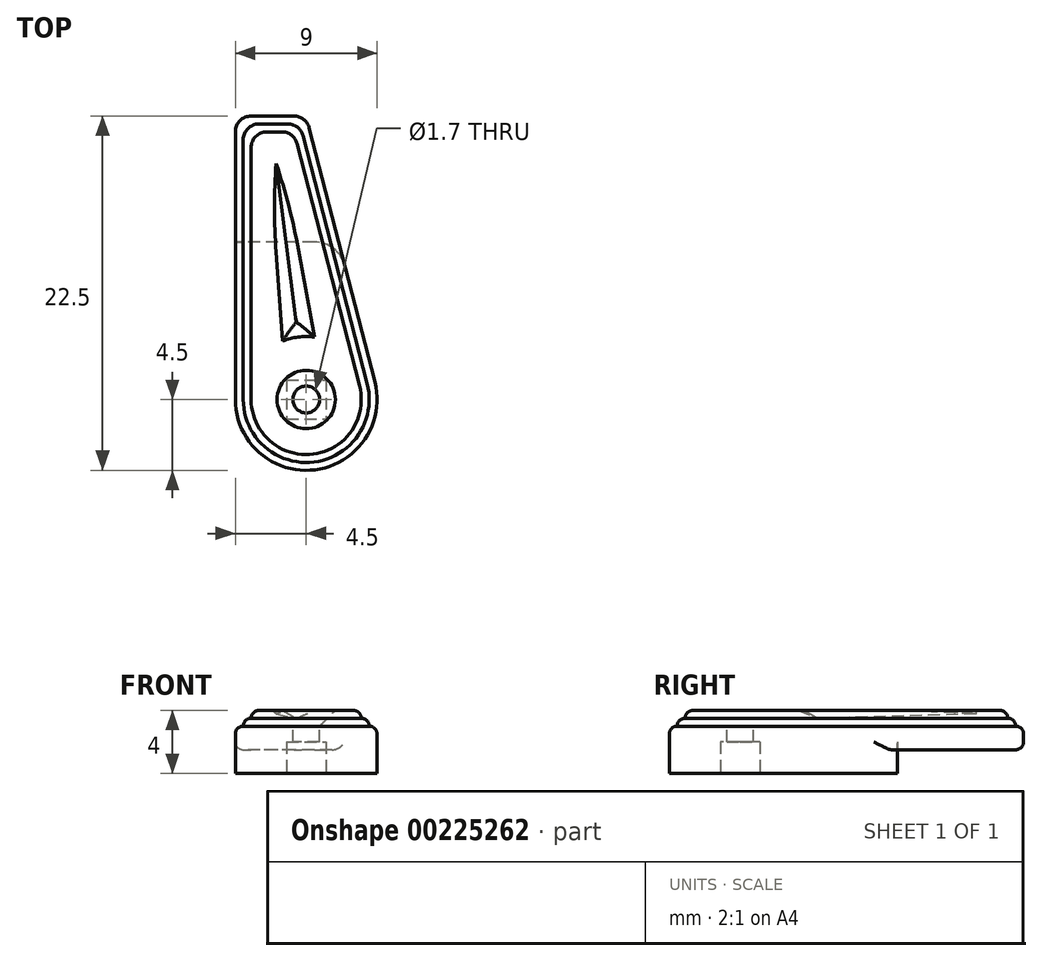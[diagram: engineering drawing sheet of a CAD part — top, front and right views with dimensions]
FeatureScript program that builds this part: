
annotation { "Feature Type Name" : "Feature", "Feature Type Description" : "" }
export const myFeature = defineFeature(function(context is Context, id is Id, definition is map)
    precondition{}
    {
        {
            var Q0;
            Q0=qCreatedBy(makeId("Top.planeOp"),FACE);
            var sketch = newSketch(context, id + "F0", { "sketchPlane" : qUnion([Q0])});
            skLineSegment(sketch, "E0.bottom", {"start": v(-1.25, 1.25) * mm, "end": v(1.25, 1.25) * mm});
            skLineSegment(sketch, "E0.top", {"start": v(-1.25, -1.25) * mm, "end": v(1.25, -1.25) * mm});
            skLineSegment(sketch, "E0.left", {"start": v(-1.25, 1.25) * mm, "end": v(-1.25, -1.25) * mm});
            skLineSegment(sketch, "E0.right", {"start": v(1.25, 1.25) * mm, "end": v(1.25, -1.25) * mm});
            skPoint(sketch, "E0.middle", {"position": v(0, 0) * mm});
            skCircle(sketch, "E1", {"center": v(0, 0) * mm, "radius": 4.5 * mm});
            skLineSegment(sketch, "E2", {"start": v(-4.5, 0) * mm, "end": v(-4.5, 18) * mm});
            skLineSegment(sketch, "E3", {"start": v(-4.5, 18) * mm, "end": v(0, 18) * mm});
            skLineSegment(sketch, "E4", {"start": v(0, 18) * mm, "end": v(4.36, 1.12) * mm});
            skSolve(sketch);
        }
        {
            var Q0;
            Q0 = qSketchRegion(id + "F0", true);
            extrude(context, id + "F1", {"entities" : qUnion([Q0]), "depth" : 3 * mm, "offsetDistance" : 25 * mm});
        }
        {
            var Q0;
            Q0=makeQuery(id+"F1.opExtrude","CAP_FACE",FACE,{"disambiguationData":[OSD([sQuery(id+"F0.wireOp",EDGE,"E0.bottom"),sQuery(id+"F0.wireOp",EDGE,"E0.top"),sQuery(id+"F0.wireOp",EDGE,"E0.left"),sQuery(id+"F0.wireOp",EDGE,"E0.right"),sQuery(id+"F0.wireOp",EDGE,"E1"),sQuery(id+"F0.wireOp",EDGE,"E2"),sQuery(id+"F0.wireOp",EDGE,"E3"),sQuery(id+"F0.wireOp",EDGE,"E4")])],"isStart":false});
            var sketch = newSketch(context, id + "F2", { "sketchPlane" : qUnion([Q0])});
            skCircle(sketch, "E5", {"center": v(0, 0) * mm, "radius": 0.85 * mm});
            skLineSegment(sketch, "E6.0", {"start": v(-3.5, 0) * mm, "end": v(-3.5, 17) * mm});
            skArc(sketch, "E6.1", {"start": v(-3.5, 0) * mm, "mid": v(0.44, -3.47) * mm, "end": v(3.39, 0.87) * mm});
            skLineSegment(sketch, "E6.2", {"start": v(-0.77, 17) * mm, "end": v(3.39, 0.88) * mm});
            skLineSegment(sketch, "E6.3", {"start": v(-3.5, 17) * mm, "end": v(-0.77, 17) * mm});
            skSolve(sketch);
        }
        {
            var Q0;
            Q0 = qSketchRegion(id + "F2", true);
            extrude(context, id + "F3", {"entities" : qUnion([Q0]), "operationType" : NewBodyOperationType.ADD, "oppositeDirection" : true, "depth" : 1 * mm, "offsetDistance" : 25 * mm});
        }
        {
            var Q0;
            Q0=makeQuery(id+"F2.imprint","IMPRINT",FACE,{"disambiguationData":[TD([[makeQuery(id+"F2.imprint","IMPRINT",EDGE,{"derivedFrom":sQuery(id+"F2.wireOp",EDGE,"E6.0")}),-1.0]])]});
            var Q1;
            Q1=makeQuery(id+"F2.imprint","IMPRINT",FACE,{"disambiguationData":[TD([[makeQuery(id+"F2.imprint","IMPRINT",EDGE,{"derivedFrom":sQuery(id+"F2.wireOp",EDGE,"E5")}),-1.0]])]});
            extrude(context, id + "F4", {"entities" : qUnion([Q0, Q1]), "operationType" : NewBodyOperationType.ADD, "depth" : 1 * mm, "offsetDistance" : 25 * mm});
        }
        {
            var Q0;
            Q0=makeQuery(id+"F3.boolean.opBoolean","MERGE",FACE,{"derivedFrom":[makeQuery(id+"F1.opExtrude","CAP_FACE",FACE,{"disambiguationData":[OSD([sQuery(id+"F0.wireOp",EDGE,"E0.bottom"),sQuery(id+"F0.wireOp",EDGE,"E0.top"),sQuery(id+"F0.wireOp",EDGE,"E0.left"),sQuery(id+"F0.wireOp",EDGE,"E0.right"),sQuery(id+"F0.wireOp",EDGE,"E1"),sQuery(id+"F0.wireOp",EDGE,"E2"),sQuery(id+"F0.wireOp",EDGE,"E3"),sQuery(id+"F0.wireOp",EDGE,"E4")])],"isStart":false}),makeQuery(id+"F3.opExtrude","CAP_FACE",FACE,{"disambiguationData":[OSD([sQuery(id+"F2.wireOp",EDGE,"E5"),sQuery(id+"F2.wireOp",EDGE,"E6.0"),sQuery(id+"F2.wireOp",EDGE,"E6.1"),sQuery(id+"F2.wireOp",EDGE,"E6.2"),sQuery(id+"F2.wireOp",EDGE,"E6.3")])],"isStart":true})]});
            var sketch = newSketch(context, id + "F5", { "sketchPlane" : qUnion([Q0])});
            skLineSegment(sketch, "E7.0", {"start": v(-0.39, 17.5) * mm, "end": v(3.87, 1) * mm});
            skLineSegment(sketch, "E7.1", {"start": v(-4, 17.5) * mm, "end": v(-0.39, 17.5) * mm});
            skLineSegment(sketch, "E7.2", {"start": v(-4, 0) * mm, "end": v(-4, 17.5) * mm});
            skArc(sketch, "E7.3", {"start": v(-4, 0) * mm, "mid": v(0.5, -3.97) * mm, "end": v(3.87, 1) * mm});
            skCircle(sketch, "E8", {"center": v(0, 0) * mm, "radius": 1 * mm});
            skSolve(sketch);
        }
        {
            var Q0;
            Q0 = qSketchRegion(id + "F5", true);
            extrude(context, id + "F6", {"entities" : qUnion([Q0]), "operationType" : NewBodyOperationType.ADD, "depth" : 0.5 * mm, "offsetDistance" : 25 * mm});
        }
        {
            var Q0;
            Q0=makeQuery(id+"F1.opExtrude","SWEPT_EDGE",EDGE,{"disambiguationData":[OSD([sQuery(id+"F0.wireOp",EDGE,"E2"),sQuery(id+"F0.wireOp",EDGE,"E3")])]});
            var Q1;
            Q1=makeQuery(id+"F1.opExtrude","SWEPT_EDGE",EDGE,{"disambiguationData":[OSD([sQuery(id+"F0.wireOp",EDGE,"E3"),sQuery(id+"F0.wireOp",EDGE,"E4")])]});
            var Q2;
            Q2=makeQuery(id+"F6.opExtrude","SWEPT_EDGE",EDGE,{"disambiguationData":[OSD([sQuery(id+"F5.wireOp",EDGE,"E7.1"),sQuery(id+"F5.wireOp",EDGE,"E7.2")])]});
            var Q3;
            Q3=makeQuery(id+"F4.opExtrude","SWEPT_EDGE",EDGE,{"disambiguationData":[OSD([sQuery(id+"F2.wireOp",EDGE,"E6.0"),sQuery(id+"F2.wireOp",EDGE,"E6.3")])]});
            var Q4;
            Q4=makeQuery(id+"F6.opExtrude","SWEPT_EDGE",EDGE,{"disambiguationData":[OSD([sQuery(id+"F5.wireOp",EDGE,"E7.0"),sQuery(id+"F5.wireOp",EDGE,"E7.1")])]});
            var Q5;
            Q5=makeQuery(id+"F4.opExtrude","SWEPT_EDGE",EDGE,{"disambiguationData":[OSD([sQuery(id+"F2.wireOp",EDGE,"E6.2"),sQuery(id+"F2.wireOp",EDGE,"E6.3")])]});
            fillet(context, id + "F7", {"entities" : qUnion([Q0, Q1, Q2, Q3, Q4, Q5]), "radius" : 1 * mm, "tangentPropagation" : true, "allowEdgeOverflow" : false});
        }
        {
            var Q0;
            Q0=makeQuery(id+"F1.opExtrude","SWEPT_FACE",FACE,{"disambiguationData":[OSD([sQuery(id+"F0.wireOp",EDGE,"E2")])]});
            var sketch = newSketch(context, id + "F8", { "sketchPlane" : qUnion([Q0])});
            skPoint(sketch, "E9.oppositeSnap0", {"position": v(-17, 1.5) * mm});
            skLineSegment(sketch, "E9.bottom", {"start": v(-18, 0) * mm, "end": v(-10, 0) * mm});
            skLineSegment(sketch, "E9.top", {"start": v(-18, 1.5) * mm, "end": v(-10, 1.5) * mm});
            skLineSegment(sketch, "E9.left", {"start": v(-18, 0) * mm, "end": v(-18, 1.5) * mm});
            skLineSegment(sketch, "E9.right", {"start": v(-10, 0) * mm, "end": v(-10, 1.5) * mm});
            skSolve(sketch);
        }
        {
            var Q0;
            Q0 = qSketchRegion(id + "F8", true);
            extrude(context, id + "F9", {"entities" : qUnion([Q0]), "operationType" : NewBodyOperationType.REMOVE, "oppositeDirection" : true, "depth" : 25 * mm, "offsetDistance" : 25 * mm});
        }
        {
            var Q0;
            Q0=makeQuery(id+"F9.boolean.opBoolean","INTERSECT",EDGE,{"derivedFrom":[makeQuery(id+"F1.opExtrude","SWEPT_FACE",FACE,{"disambiguationData":[OSD([sQuery(id+"F0.wireOp",EDGE,"E4")])]}),makeQuery(id+"F9.opExtrude","SWEPT_FACE",FACE,{"disambiguationData":[OSD([sQuery(id+"F8.wireOp",EDGE,"E9.right")])]})]});
            var Q1;
            Q1=makeQuery(id+"F9.boolean.opBoolean","COPY",EDGE,{"derivedFrom":makeQuery(id+"F9.opExtrude","CAP_EDGE",EDGE,{"disambiguationData":[OSD([sQuery(id+"F8.wireOp",EDGE,"E9.right")])],"isStart":true})});
            fillet(context, id + "F10", {"entities" : qUnion([Q0, Q1]), "radius" : 2 * mm, "tangentPropagation" : true, "allowEdgeOverflow" : false});
        }
        {
            var Q0;
            Q0=makeQuery(id+"F9.boolean.opBoolean","INTERSECT",EDGE,{"derivedFrom":[makeQuery(id+"F1.opExtrude","SWEPT_FACE",FACE,{"disambiguationData":[OSD([sQuery(id+"F0.wireOp",EDGE,"E4")])]}),makeQuery(id+"F9.opExtrude","SWEPT_FACE",FACE,{"disambiguationData":[OSD([sQuery(id+"F8.wireOp",EDGE,"E9.top")])]})]});
            var Q1;
            Q1=makeQuery(id+"F1.opExtrude","CAP_EDGE",EDGE,{"disambiguationData":[OSD([sQuery(id+"F0.wireOp",EDGE,"E4")])],"isStart":false});
            var Q2;
            Q2=makeQuery(id+"F6.opExtrude","CAP_EDGE",EDGE,{"disambiguationData":[OSD([sQuery(id+"F5.wireOp",EDGE,"E7.0")])],"isStart":false});
            var Q3;
            Q3=makeQuery(id+"F4.opExtrude","CAP_EDGE",EDGE,{"disambiguationData":[OSD([sQuery(id+"F2.wireOp",EDGE,"E6.2")])],"isStart":false});
            fillet(context, id + "F11", {"entities" : qUnion([Q0, Q1, Q2, Q3]), "radius" : 0.5 * mm, "tangentPropagation" : true, "allowEdgeOverflow" : false});
        }
        {
            var Q0;
            Q0=makeQuery(id+"F4.opExtrude","CAP_EDGE",EDGE,{"disambiguationData":[OSD([sQuery(id+"F2.wireOp",EDGE,"E5")])],"isStart":false});
            chamfer(context, id + "F12", {"entities" : qUnion([Q0]), "width" : 1 * mm, "tangentPropagation" : true});
        }
        {
            var Q0;
            Q0=makeQuery(id+"F4.opExtrude","CAP_FACE",FACE,{"disambiguationData":[OSD([sQuery(id+"F2.wireOp",EDGE,"E5"),sQuery(id+"F2.wireOp",EDGE,"E6.0"),sQuery(id+"F2.wireOp",EDGE,"E6.1"),sQuery(id+"F2.wireOp",EDGE,"E6.2"),sQuery(id+"F2.wireOp",EDGE,"E6.3")])],"isStart":false});
            var sketch = newSketch(context, id + "F13", { "sketchPlane" : qUnion([Q0])});
            skArc(sketch, "E10", {"start": v(-1.5, 3.7) * mm, "mid": v(-0.5, 3.97) * mm, "end": v(0.53, 3.97) * mm});
            skLineSegment(sketch, "E11", {"start": v(-1.5, 3.7) * mm, "end": v(-1.91, 9.35) * mm});
            skLineSegment(sketch, "E12", {"start": v(-0.49, 9.48) * mm, "end": v(0.53, 3.97) * mm});
            skArc(sketch, "E13", {"start": v(-1.91, 15) * mm, "mid": v(-2.01, 12.18) * mm, "end": v(-1.91, 9.35) * mm});
            skArc(sketch, "E14", {"start": v(-0.49, 9.48) * mm, "mid": v(-1.1, 12.27) * mm, "end": v(-1.91, 15) * mm});
            skSolve(sketch);
        }
        {
            var Q0;
            Q0 = qSketchRegion(id + "F13", true);
            extrude(context, id + "F14", {"entities" : qUnion([Q0]), "operationType" : NewBodyOperationType.REMOVE, "oppositeDirection" : true, "depth" : 0.5 * mm, "offsetDistance" : 25 * mm});
        }
        {
            var Q0;
            Q0=makeQuery(id+"F14.boolean.opBoolean","COPY",EDGE,{"derivedFrom":makeQuery(id+"F14.opExtrude","CAP_EDGE",EDGE,{"disambiguationData":[OSD([sQuery(id+"F13.wireOp",EDGE,"E12")])],"isStart":false})});
            var Q1;
            Q1=makeQuery(id+"F14.boolean.opBoolean","COPY",EDGE,{"derivedFrom":makeQuery(id+"F14.opExtrude","CAP_EDGE",EDGE,{"disambiguationData":[OSD([sQuery(id+"F13.wireOp",EDGE,"E11")])],"isStart":false})});
            var Q2;
            Q2=makeQuery(id+"F14.boolean.opBoolean","COPY",EDGE,{"derivedFrom":makeQuery(id+"F14.opExtrude","CAP_EDGE",EDGE,{"disambiguationData":[OSD([sQuery(id+"F13.wireOp",EDGE,"E10")])],"isStart":false})});
            var Q3;
            Q3=makeQuery(id+"F14.boolean.opBoolean","COPY",EDGE,{"derivedFrom":makeQuery(id+"F14.opExtrude","CAP_EDGE",EDGE,{"disambiguationData":[OSD([sQuery(id+"F13.wireOp",EDGE,"E13")])],"isStart":false})});
            var Q4;
            Q4=makeQuery(id+"F14.boolean.opBoolean","COPY",EDGE,{"derivedFrom":makeQuery(id+"F14.opExtrude","CAP_EDGE",EDGE,{"disambiguationData":[OSD([sQuery(id+"F13.wireOp",EDGE,"E14")])],"isStart":false})});
            chamfer(context, id + "F15", {"entities" : qUnion([Q0, Q1, Q2, Q3, Q4]), "chamferType" : ChamferType.OFFSET_ANGLE, "width" : 0.5 * mm, "oppositeDirection" : false, "angle" : 62.1 * degree, "tangentPropagation" : true});
        }
    });
